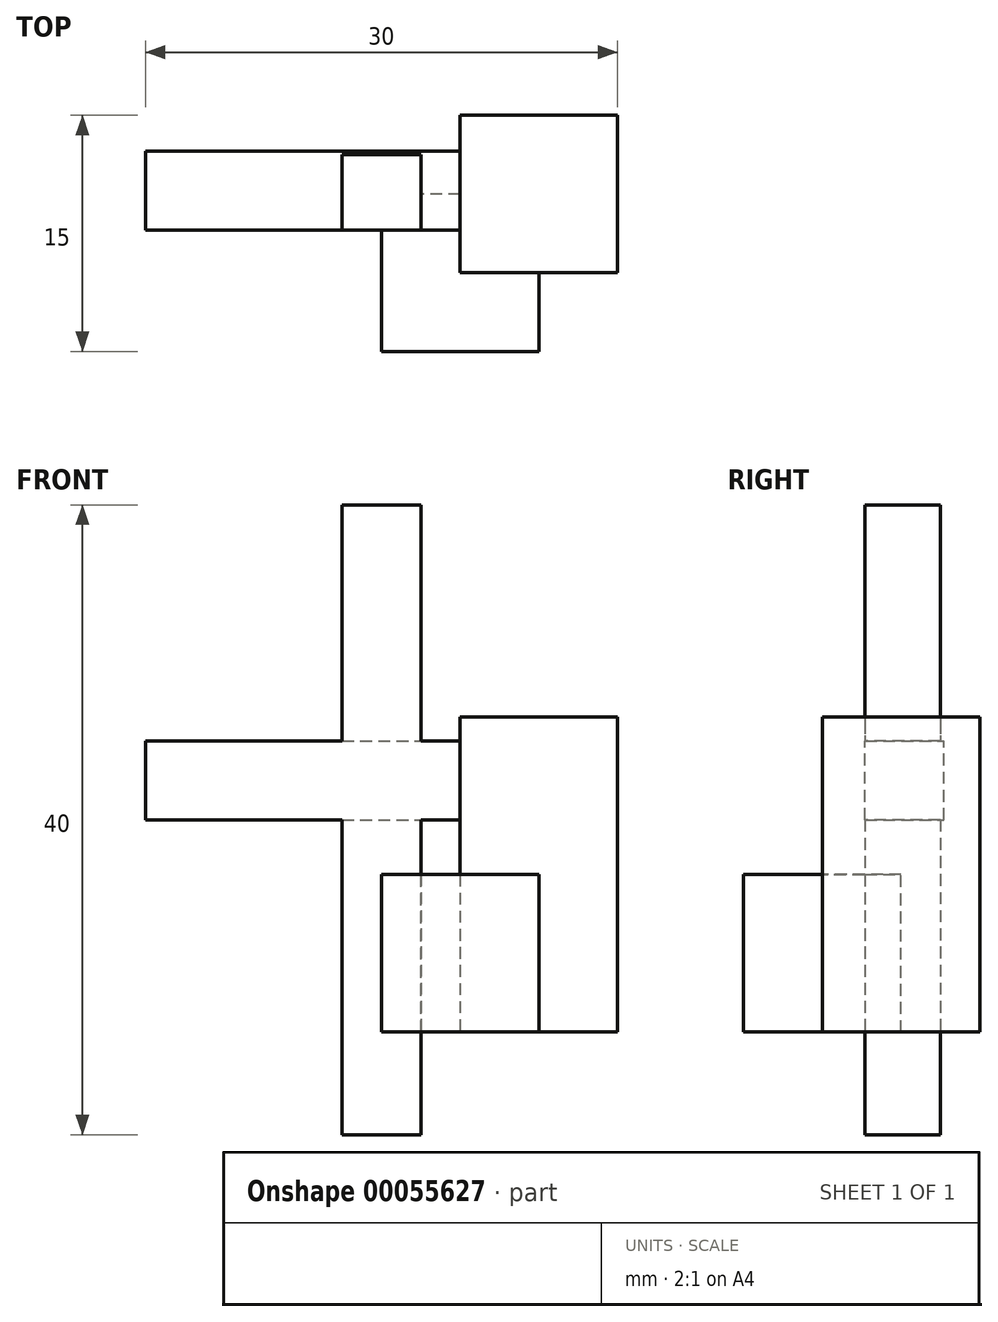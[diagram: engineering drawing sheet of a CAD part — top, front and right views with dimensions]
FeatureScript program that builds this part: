
annotation { "Feature Type Name" : "Feature", "Feature Type Description" : "" }
export const myFeature = defineFeature(function(context is Context, id is Id, definition is map)
    precondition{}
    {
        {
            var Q0;
            Q0=qCreatedBy(makeId("Top.planeOp"),FACE);
            var sketch = newSketch(context, id + "F0", { "sketchPlane" : qUnion([Q0])});
            skLineSegment(sketch, "E0.rect.bottom", {"start": v(5, -5) * mm, "end": v(-5, -5) * mm});
            skLineSegment(sketch, "E0.rect.top", {"start": v(5, 5) * mm, "end": v(-5, 5) * mm});
            skLineSegment(sketch, "E0.rect.left", {"start": v(5, -5) * mm, "end": v(5, 5) * mm});
            skLineSegment(sketch, "E0.rect.right", {"start": v(-5, -5) * mm, "end": v(-5, 5) * mm});
            skPoint(sketch, "E0.rect.middle", {"position": v(0, 0) * mm});
            skLineSegment(sketch, "E1.rect.bottom", {"start": v(0, 0) * mm, "end": v(10, 0) * mm});
            skLineSegment(sketch, "E1.rect.top", {"start": v(0, 10) * mm, "end": v(10, 10) * mm});
            skLineSegment(sketch, "E1.rect.left", {"start": v(0, 0) * mm, "end": v(0, 10) * mm});
            skLineSegment(sketch, "E1.rect.right", {"start": v(10, 0) * mm, "end": v(10, 10) * mm});
            skPoint(sketch, "E1.rect.middle", {"position": v(5, 5) * mm});
            skSolve(sketch);
        }
        {
            var Q0;
            Q0=makeQuery(id+"F0.imprint","IMPRINT",FACE,{"disambiguationData":[TD([[makeQuery(id+"F0.imprint","IMPRINT",EDGE,{"derivedFrom":sQuery(id+"F0.wireOp",EDGE,"E0.rect.bottom")}),-1.0]])]});
            var Q1;
            {var subQ0=sQuery(id+"F0.wireOp",EDGE,"E0.rect.left");var subQ1=sQuery(id+"F0.wireOp",EDGE,"E0.rect.top");var subQ2=makeQuery(id+"F0.imprint","INTERSECT",VERTEX,{"derivedFrom":[subQ1,subQ0]});Q1=makeQuery(id+"F0.imprint","IMPRINT",FACE,{"disambiguationData":[TD([[makeQuery(id+"F0.imprint","IMPRINT",EDGE,{"disambiguationData":[TD([[subQ2,-1.0]])],"derivedFrom":subQ1}),1.0]])]});}
            extrude(context, id + "F1", {"entities" : qUnion([Q0, Q1]), "depth" : 10 * mm});
        }
        {
            var Q0;
            {var subQ0=sQuery(id+"F0.wireOp",EDGE,"E1.rect.top");Q0=makeQuery(id+"F0.imprint","IMPRINT",FACE,{"disambiguationData":[TD([[makeQuery(id+"F0.imprint","IMPRINT",EDGE,{"derivedFrom":subQ0}),-1.0]])]});}
            var Q1;
            {var subQ0=sQuery(id+"F0.wireOp",EDGE,"E0.rect.left");var subQ1=sQuery(id+"F0.wireOp",EDGE,"E0.rect.top");var subQ2=makeQuery(id+"F0.imprint","INTERSECT",VERTEX,{"derivedFrom":[subQ1,subQ0]});Q1=makeQuery(id+"F0.imprint","IMPRINT",FACE,{"disambiguationData":[TD([[makeQuery(id+"F0.imprint","IMPRINT",EDGE,{"disambiguationData":[TD([[subQ2,-1.0]])],"derivedFrom":subQ1}),1.0]])]});}
            extrude(context, id + "F2", {"entities" : qUnion([Q0, Q1]), "operationType" : NewBodyOperationType.ADD, "depth" : 20 * mm});
        }
        {
            var Q0;
            Q0=makeQuery(id+"F2.opExtrude","SWEPT_FACE",FACE,{"disambiguationData":[OSD([sQuery(id+"F0.wireOp",EDGE,"E1.rect.left")])]});
            var sketch = newSketch(context, id + "F3", { "sketchPlane" : qUnion([Q0])});
            skLineSegment(sketch, "E2.rect.bottom", {"start": v(-2.72, 13.48) * mm, "end": v(-7.72, 13.48) * mm});
            skLineSegment(sketch, "E2.rect.top", {"start": v(-2.72, 18.48) * mm, "end": v(-7.72, 18.48) * mm});
            skLineSegment(sketch, "E2.rect.left", {"start": v(-2.72, 13.48) * mm, "end": v(-2.72, 18.48) * mm});
            skLineSegment(sketch, "E2.rect.right", {"start": v(-7.72, 13.48) * mm, "end": v(-7.72, 18.48) * mm});
            skPoint(sketch, "E2.rect.middle", {"position": v(-5.22, 15.98) * mm});
            skSolve(sketch);
        }
        {
            var Q0;
            Q0=makeQuery(id+"F3.imprint","IMPRINT",FACE,{"disambiguationData":[TD([[makeQuery(id+"F3.imprint","IMPRINT",EDGE,{"derivedFrom":sQuery(id+"F3.wireOp",EDGE,"E2.rect.bottom")}),-1.0]])]});
            extrude(context, id + "F4", {"entities" : qUnion([Q0]), "depth" : 20 * mm});
        }
        {
            var Q0;
            Q0=makeQuery(id+"F4.opExtrude","SWEPT_FACE",FACE,{"disambiguationData":[OSD([sQuery(id+"F3.wireOp",EDGE,"E2.rect.bottom")])]});
            var sketch = newSketch(context, id + "F5", { "sketchPlane" : qUnion([Q0])});
            skPoint(sketch, "E3.0", {"position": v(-5, -5) * mm});
            skLineSegment(sketch, "E4.rect.bottom", {"start": v(-7.5, -7.5) * mm, "end": v(-2.5, -7.5) * mm});
            skLineSegment(sketch, "E4.rect.top", {"start": v(-7.5, -2.5) * mm, "end": v(-2.5, -2.5) * mm});
            skLineSegment(sketch, "E4.rect.left", {"start": v(-7.5, -7.5) * mm, "end": v(-7.5, -2.5) * mm});
            skLineSegment(sketch, "E4.rect.right", {"start": v(-2.5, -7.5) * mm, "end": v(-2.5, -2.5) * mm});
            skSolve(sketch);
        }
        {
            var Q0;
            {var subQ0=sQuery(id+"F5.wireOp",EDGE,"E4.rect.bottom");Q0=makeQuery(id+"F5.imprint","IMPRINT",FACE,{"disambiguationData":[TD([[makeQuery(id+"F5.imprint","IMPRINT",EDGE,{"derivedFrom":subQ0}),1.0]])]});}
            extrude(context, id + "F6", {"entities" : qUnion([Q0]), "operationType" : NewBodyOperationType.ADD, "endBound" : BoundingType.SYMMETRIC, "oppositeDirection" : true, "depth" : 40 * mm});
        }
    });
